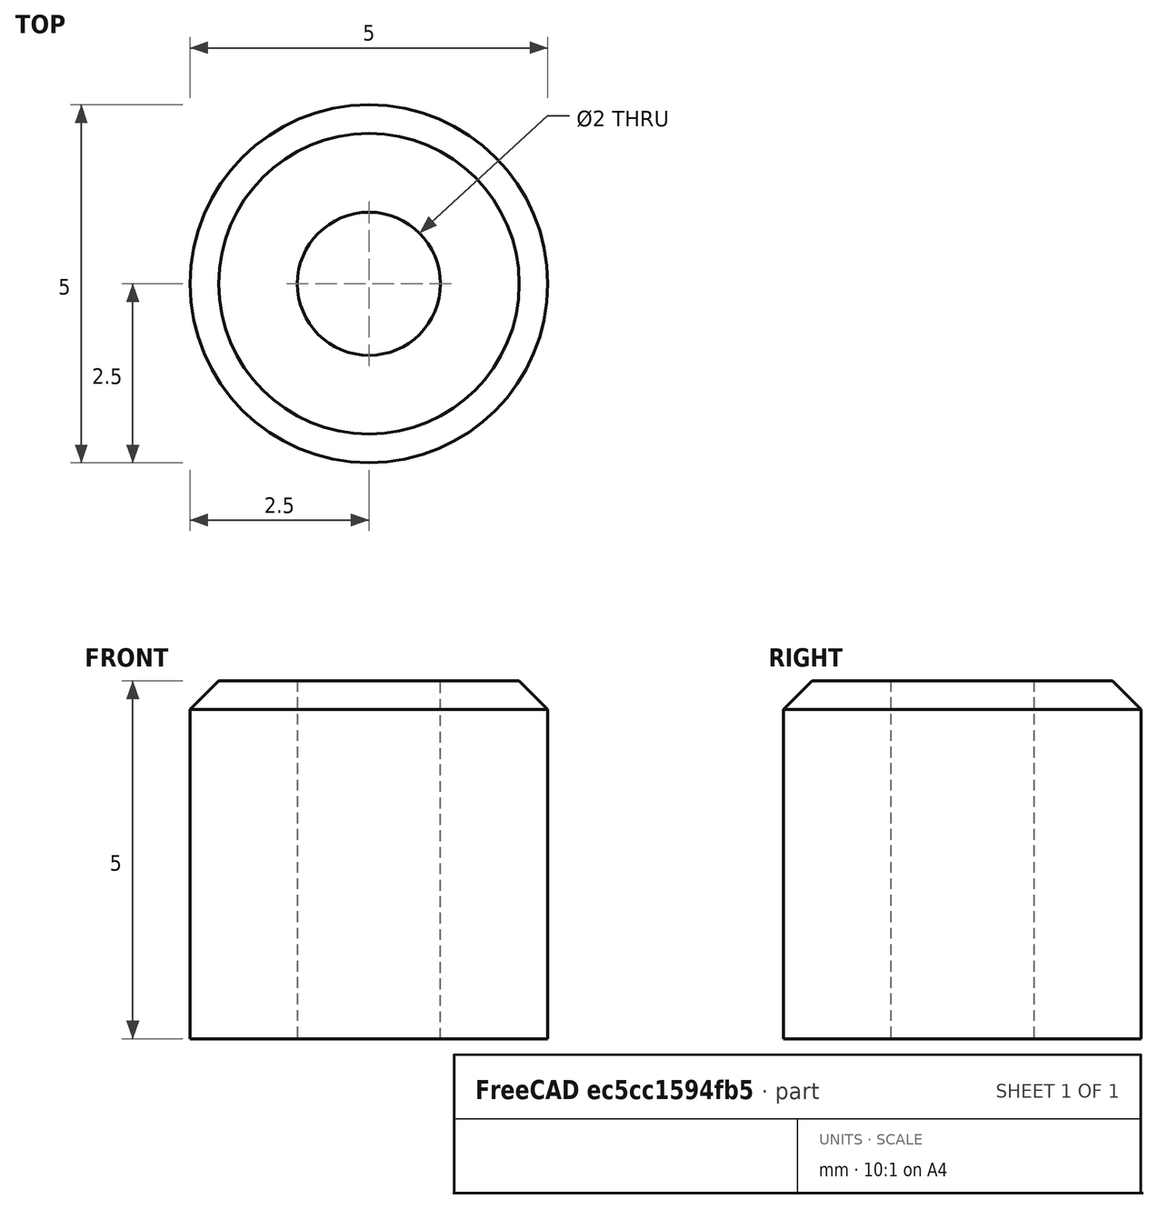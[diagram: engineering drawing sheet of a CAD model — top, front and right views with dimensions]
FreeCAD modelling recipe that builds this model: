
FCSTD DOCUMENT  (FreeCAD 0.18R4 (GitTag))
Label: Shoulder_Joint_Ball_Bearing_Pin
License: CreativeCommons Attribution-NonCommercial
LicenseURL: http://creativecommons.org/licenses/by-nc/4.0/
objects: Sketcher::SketchObject×1, PartDesign::Pad×1, PartDesign::Chamfer×1, PartDesign::Body×1
note: 5 computed .brp shape members not serialized (recipe doc carries the construction recipe); baked Part::Feature solids carry a one-line shape summary decoded from their .brp

FEATURE [Sketcher::SketchObject] Sketch
  MapMode = 5
  Support = -> [XY_Plane]
  sketch-geometry (2):
    g0: Circle CenterX=0 CenterY=0 CenterZ=0 NormalX=0 NormalY=0 NormalZ=1 AngleXU=0 Radius=2.5
    g1: Circle CenterX=0 CenterY=0 CenterZ=0 NormalX=0 NormalY=0 NormalZ=1 AngleXU=0 Radius=1
  constraints (4):
    c: Coincident(g0,g-1)
    c: Coincident(g1,g0)
    c: Radius(g0) = 2.5
    c: Radius(g1) = 1
FEATURE [PartDesign::Pad] Pad  label="Ball Bearing Pin"
  Length = 5
  Length2 = 100
  Profile = -> Sketch
  Type = 0
FEATURE [PartDesign::Chamfer] Chamfer  label="Smooth Pinhead"
  Base = -> Pad [Edge3]
  BaseFeature = -> Pad
  Size = 0.4
FEATURE [PartDesign::Body] Body  label="Shoulder_Joint_Ball_Bearing_Pin"
  Group = -> [Sketch,Pad,Chamfer]
  Origin = -> Origin
  Tip = -> Chamfer
